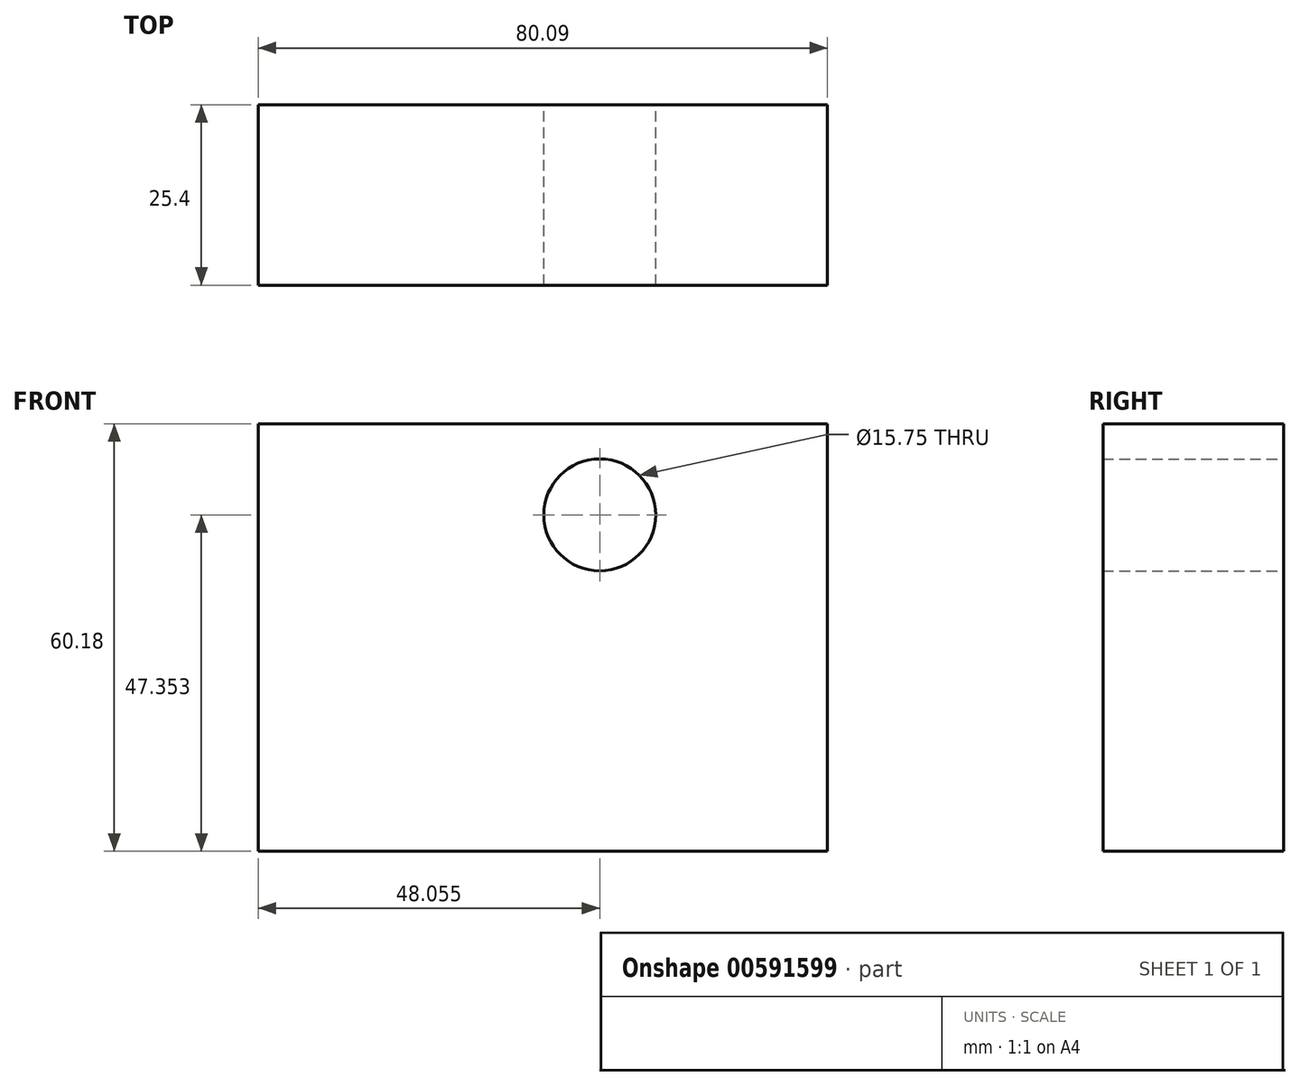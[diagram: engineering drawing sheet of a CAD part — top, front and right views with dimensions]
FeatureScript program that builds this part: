
annotation { "Feature Type Name" : "Feature", "Feature Type Description" : "" }
export const myFeature = defineFeature(function(context is Context, id is Id, definition is map)
    precondition{}
    {
        {
            var Q0;
            Q0=qCreatedBy(makeId("Front.planeOp"),FACE);
            var sketch = newSketch(context, id + "F0", { "sketchPlane" : qUnion([Q0])});
            skLineSegment(sketch, "E0.bottom", {"start": v(-38.71, 35.55) * mm, "end": v(41.38, 35.55) * mm});
            skLineSegment(sketch, "E0.top", {"start": v(-38.71, -24.63) * mm, "end": v(41.38, -24.63) * mm});
            skLineSegment(sketch, "E0.left", {"start": v(-38.71, 35.55) * mm, "end": v(-38.71, -24.63) * mm});
            skLineSegment(sketch, "E0.right", {"start": v(41.38, 35.55) * mm, "end": v(41.38, -24.63) * mm});
            skCircle(sketch, "E1", {"center": v(9.34, 22.72) * mm, "radius": 7.87 * mm});
            skSolve(sketch);
        }
        {
            var Q0;
            Q0 = qSketchRegion(id + "F0", true);
            extrude(context, id + "F1", {"entities" : qUnion([Q0]), "depth" : 25.4 * mm, "offsetDistance" : 25.4 * mm});
        }
    });
